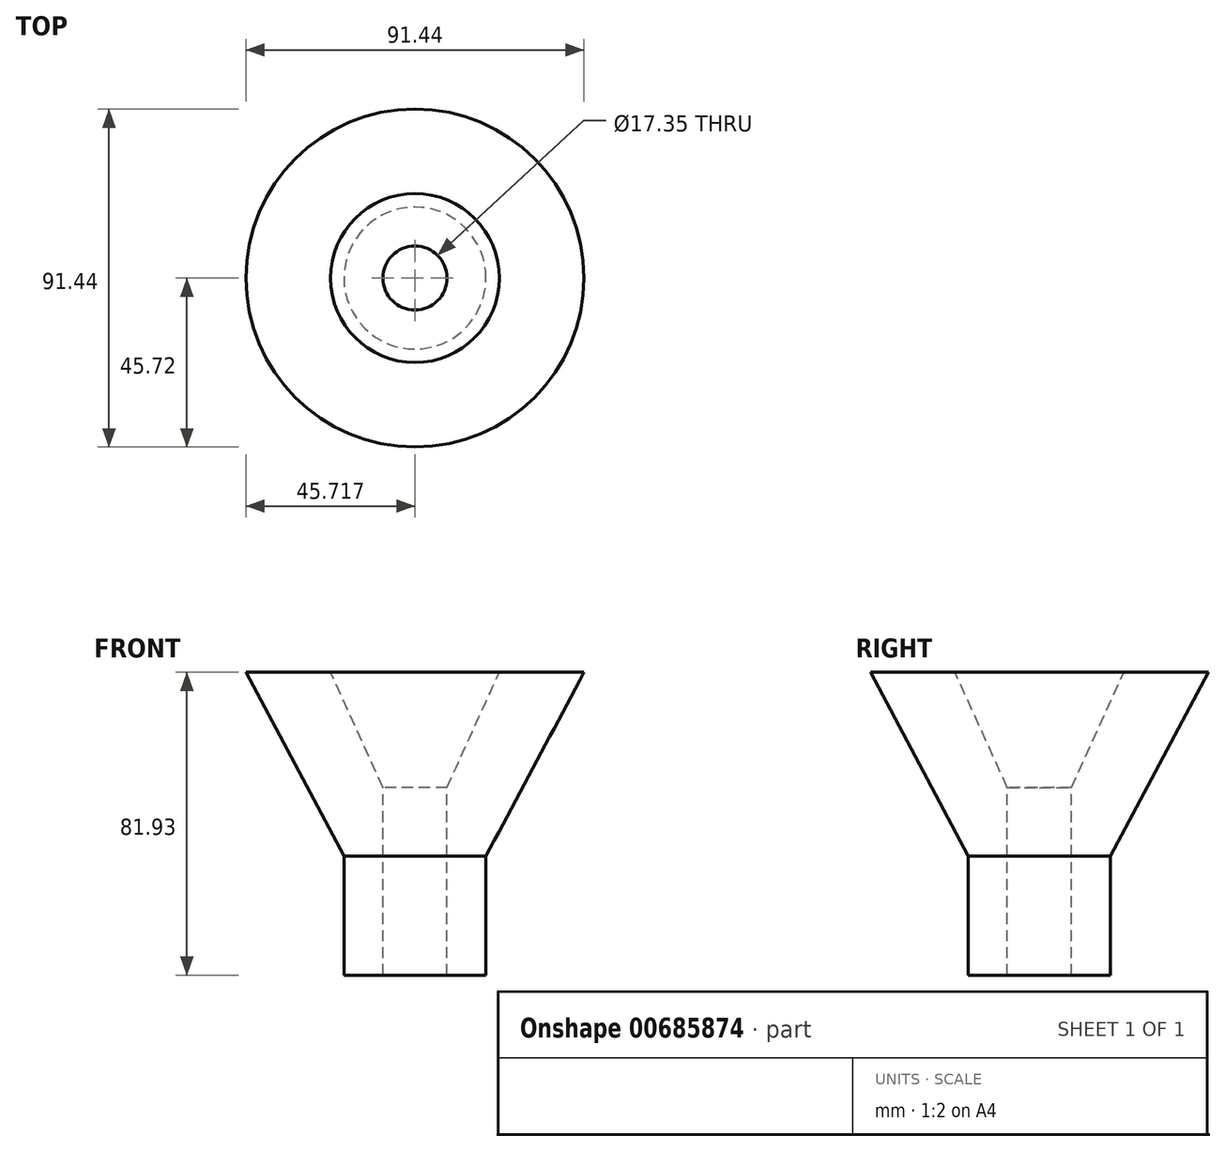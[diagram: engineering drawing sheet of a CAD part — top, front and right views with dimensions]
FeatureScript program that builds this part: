
annotation { "Feature Type Name" : "Feature", "Feature Type Description" : "" }
export const myFeature = defineFeature(function(context is Context, id is Id, definition is map)
    precondition{}
    {
        {
            var Q0;
            Q0=qCreatedBy(makeId("Front.planeOp"),FACE);
            var sketch = newSketch(context, id + "F0", { "sketchPlane" : qUnion([Q0])});
            skLineSegment(sketch, "E0", {"start": v(4.15, 6.47) * mm, "end": v(4.15, -25.29) * mm});
            skLineSegment(sketch, "E1", {"start": v(4.15, -25.29) * mm, "end": v(23.37, -25.29) * mm});
            skLineSegment(sketch, "E2", {"start": v(23.37, -25.29) * mm, "end": v(23.37, 6.88) * mm});
            skLineSegment(sketch, "E3", {"start": v(4.15, 6.47) * mm, "end": v(27, 56.64) * mm});
            skLineSegment(sketch, "E4", {"start": v(27, 56.64) * mm, "end": v(49.87, 56.64) * mm});
            skLineSegment(sketch, "E5", {"start": v(49.87, 56.64) * mm, "end": v(23.37, 6.88) * mm});
            skSolve(sketch);
        }
        {
            var Q0;
            Q0=makeQuery(id+"F0.imprint","IMPRINT",FACE,{"disambiguationData":[TD([[makeQuery(id+"F0.imprint","IMPRINT",EDGE,{"derivedFrom":sQuery(id+"F0.wireOp",EDGE,"E0")}),1.0]])]});
            var Q1;
            Q1=sQuery(id+"F0.wireOp",EDGE,"E0");
            revolve(context, id + "F1", {"entities" : qUnion([Q0]), "axis" : qUnion([Q1]), "revolveType" : RevolveType.FULL});
        }
        {
            var Q0;
            Q0=makeQuery(id+"F1.opRevolve","SWEPT_FACE",FACE,{"disambiguationData":[OSD([sQuery(id+"F0.wireOp",EDGE,"E1")])]});
            extrude(context, id + "F2", {"entities" : qUnion([Q0]), "operationType" : NewBodyOperationType.REMOVE, "oppositeDirection" : true, "depth" : 50.8 * mm, "offsetDistance" : 25.4 * mm});
        }
        {
            var Q0;
            Q0=makeQuery(id+"F2.boolean.opBoolean","COPY",FACE,{"derivedFrom":makeQuery(id+"F2.opExtrude","CAP_FACE",FACE,{"disambiguationData":[OSD([sQuery(id+"F0.wireOp",EDGE,"E1")])],"isStart":false})});
            extrude(context, id + "F3", {"entities" : qUnion([Q0]), "operationType" : NewBodyOperationType.ADD, "depth" : 50.8 * mm, "offsetDistance" : 25.4 * mm});
        }
    });
